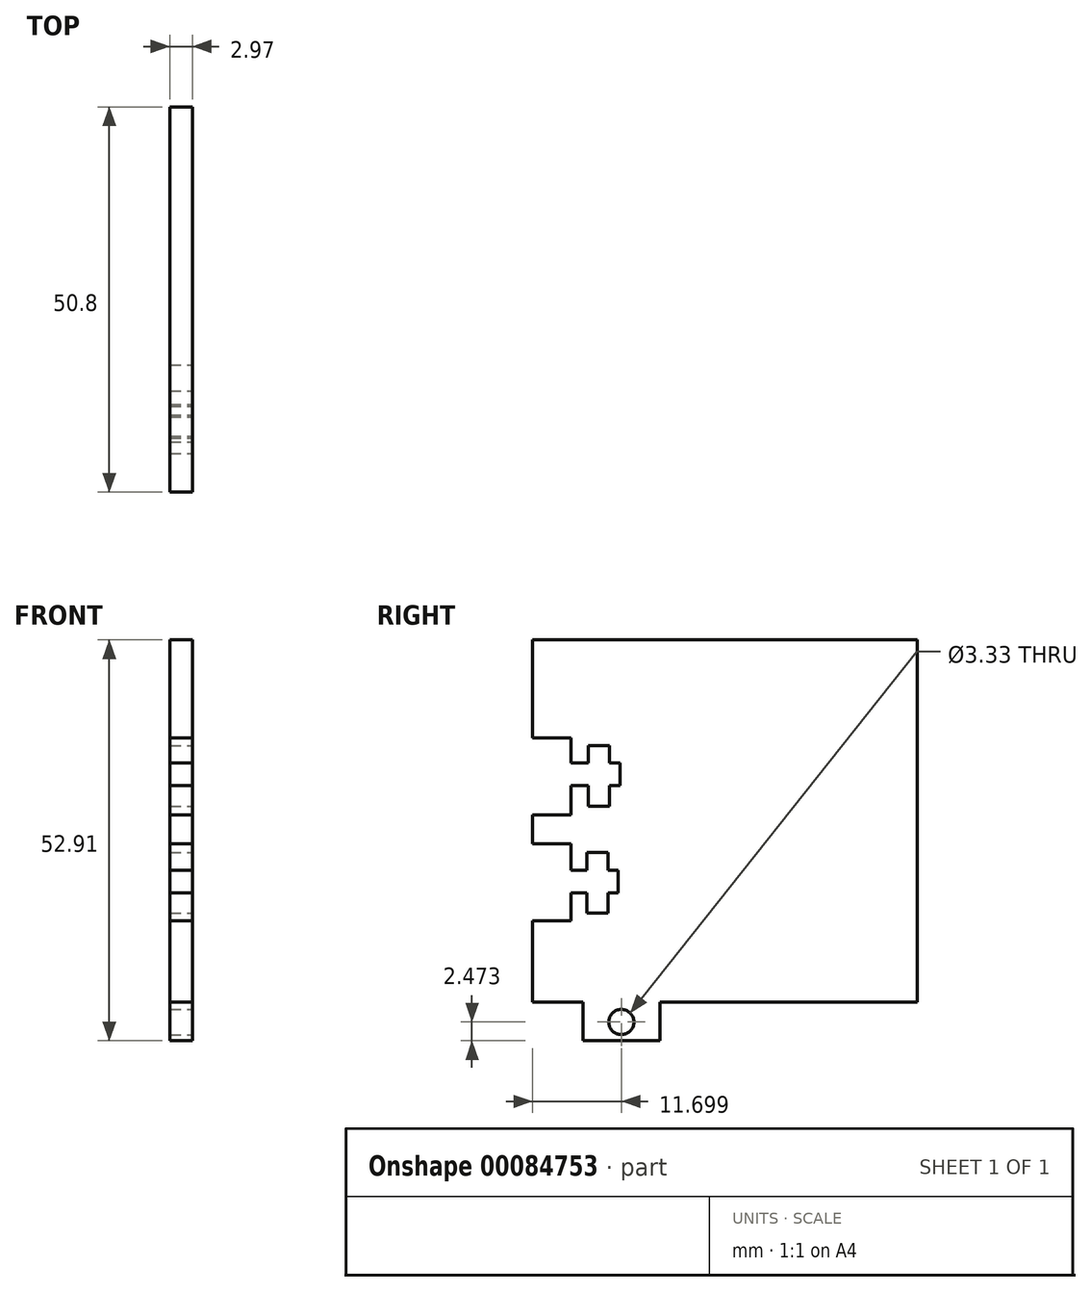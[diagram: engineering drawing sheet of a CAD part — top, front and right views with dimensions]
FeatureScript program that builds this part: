
annotation { "Feature Type Name" : "Feature", "Feature Type Description" : "" }
export const myFeature = defineFeature(function(context is Context, id is Id, definition is map)
    precondition{}
    {
        {
            var Q0;
            Q0=qCreatedBy(makeId("Right.planeOp"),FACE);
            var sketch = newSketch(context, id + "F0", { "sketchPlane" : qUnion([Q0])});
            skLineSegment(sketch, "E0.bottom", {"start": v(25.4, 25.4) * mm, "end": v(-25.4, 25.4) * mm});
            skLineSegment(sketch, "E0.top", {"start": v(25.4, -25.4) * mm, "end": v(-25.4, -25.4) * mm});
            skLineSegment(sketch, "E0.left", {"start": v(25.4, 25.4) * mm, "end": v(25.4, -25.4) * mm});
            skLineSegment(sketch, "E0.right", {"start": v(-25.4, 25.4) * mm, "end": v(-25.4, -25.4) * mm});
            skPoint(sketch, "E0.middle", {"position": v(0, 0) * mm});
            skSolve(sketch);
        }
        {
            var Q0;
            Q0 = qSketchRegion(id + "F0", true);
            extrude(context, id + "F1", {"entities" : qUnion([Q0]), "depth" : 2.97 * mm});
        }
        {
            var Q0;
            Q0=makeQuery(id+"F1.opExtrude","CAP_FACE",FACE,{"disambiguationData":[OSD([sQuery(id+"F0.wireOp",EDGE,"E0.bottom"),sQuery(id+"F0.wireOp",EDGE,"E0.top"),sQuery(id+"F0.wireOp",EDGE,"E0.left"),sQuery(id+"F0.wireOp",EDGE,"E0.right")])],"isStart":false});
            var sketch = newSketch(context, id + "F2", { "sketchPlane" : qUnion([Q0])});
            skLineSegment(sketch, "E1.bottom", {"start": v(-25.4, 12.46) * mm, "end": v(-20.32, 12.46) * mm});
            skLineSegment(sketch, "E1.top", {"start": v(-25.4, 2.3) * mm, "end": v(-20.32, 2.3) * mm});
            skLineSegment(sketch, "E1.left", {"start": v(-25.4, 12.46) * mm, "end": v(-25.4, 2.3) * mm});
            skLineSegment(sketch, "E1.right", {"start": v(-20.32, 12.46) * mm, "end": v(-20.32, 2.3) * mm});
            skLineSegment(sketch, "E2.bottom", {"start": v(-25.4, -1.5) * mm, "end": v(-20.32, -1.5) * mm});
            skLineSegment(sketch, "E2.top", {"start": v(-25.4, -11.67) * mm, "end": v(-20.32, -11.67) * mm});
            skLineSegment(sketch, "E2.left", {"start": v(-25.4, -1.5) * mm, "end": v(-25.4, -11.67) * mm});
            skLineSegment(sketch, "E2.right", {"start": v(-20.32, -1.5) * mm, "end": v(-20.32, -11.67) * mm});
            skSolve(sketch);
        }
        {
            var Q0;
            Q0 = qSketchRegion(id + "F2", true);
            extrude(context, id + "F3", {"entities" : qUnion([Q0]), "operationType" : NewBodyOperationType.REMOVE, "endBound" : BoundingType.THROUGH_ALL, "oppositeDirection" : true, "depth" : 25.4 * mm});
        }
        {
            var Q0;
            Q0=makeQuery(id+"F1.opExtrude","CAP_FACE",FACE,{"disambiguationData":[OSD([sQuery(id+"F0.wireOp",EDGE,"E0.bottom"),sQuery(id+"F0.wireOp",EDGE,"E0.top"),sQuery(id+"F0.wireOp",EDGE,"E0.left"),sQuery(id+"F0.wireOp",EDGE,"E0.right")])],"isStart":false});
            var sketch = newSketch(context, id + "F4", { "sketchPlane" : qUnion([Q0])});
            skLineSegment(sketch, "E3.bottom", {"start": v(-20.32, 9.15) * mm, "end": v(-13.87, 9.15) * mm});
            skLineSegment(sketch, "E3.top", {"start": v(-20.32, 6.17) * mm, "end": v(-13.87, 6.17) * mm});
            skLineSegment(sketch, "E3.left", {"start": v(-20.32, 9.15) * mm, "end": v(-20.32, 6.17) * mm});
            skLineSegment(sketch, "E3.right", {"start": v(-13.87, 9.15) * mm, "end": v(-13.87, 6.17) * mm});
            skLineSegment(sketch, "E4.bottom", {"start": v(-15.25, 11.45) * mm, "end": v(-18.04, 11.45) * mm});
            skLineSegment(sketch, "E4.top", {"start": v(-15.25, 3.45) * mm, "end": v(-18.04, 3.45) * mm});
            skLineSegment(sketch, "E4.left", {"start": v(-15.25, 11.45) * mm, "end": v(-15.25, 3.45) * mm});
            skLineSegment(sketch, "E4.right", {"start": v(-18.04, 11.45) * mm, "end": v(-18.04, 3.45) * mm});
            skLineSegment(sketch, "E5.bottom", {"start": v(-20.55, -4.98) * mm, "end": v(-14.1, -4.98) * mm});
            skLineSegment(sketch, "E5.top", {"start": v(-20.55, -7.96) * mm, "end": v(-14.1, -7.96) * mm});
            skLineSegment(sketch, "E5.left", {"start": v(-20.55, -4.98) * mm, "end": v(-20.55, -7.96) * mm});
            skLineSegment(sketch, "E5.right", {"start": v(-14.1, -4.98) * mm, "end": v(-14.1, -7.96) * mm});
            skLineSegment(sketch, "E6.bottom", {"start": v(-15.48, -2.68) * mm, "end": v(-18.28, -2.68) * mm});
            skLineSegment(sketch, "E6.top", {"start": v(-15.48, -10.69) * mm, "end": v(-18.28, -10.69) * mm});
            skLineSegment(sketch, "E6.left", {"start": v(-15.48, -2.68) * mm, "end": v(-15.48, -10.69) * mm});
            skLineSegment(sketch, "E6.right", {"start": v(-18.28, -2.68) * mm, "end": v(-18.28, -10.69) * mm});
            skSolve(sketch);
        }
        {
            var Q0;
            {var subQ0=sQuery(id+"F4.wireOp",EDGE,"E3.left");Q0=makeQuery(id+"F4.imprint","IMPRINT",FACE,{"disambiguationData":[TD([[makeQuery(id+"F4.imprint","IMPRINT",EDGE,{"derivedFrom":subQ0}),1.0]])]});}
            var Q1;
            {var subQ0=sQuery(id+"F4.wireOp",EDGE,"E4.right");var subQ1=sQuery(id+"F4.wireOp",EDGE,"E3.bottom");var subQ2=makeQuery(id+"F4.imprint","INTERSECT",VERTEX,{"derivedFrom":[subQ1,subQ0]});Q1=makeQuery(id+"F4.imprint","IMPRINT",FACE,{"disambiguationData":[TD([[makeQuery(id+"F4.imprint","IMPRINT",EDGE,{"disambiguationData":[TD([[subQ2,-1.0]])],"derivedFrom":subQ1}),-1.0]])]});}
            var Q2;
            {var subQ0=sQuery(id+"F4.wireOp",EDGE,"E3.right");Q2=makeQuery(id+"F4.imprint","IMPRINT",FACE,{"disambiguationData":[TD([[makeQuery(id+"F4.imprint","IMPRINT",EDGE,{"derivedFrom":subQ0}),-1.0]])]});}
            var Q3;
            {var subQ5=sQuery(id+"F4.wireOp",EDGE,"E4.bottom");Q3=makeQuery(id+"F4.imprint","IMPRINT",FACE,{"disambiguationData":[TD([[makeQuery(id+"F4.imprint","IMPRINT",EDGE,{"derivedFrom":subQ5}),1.0]])]});}
            var Q4;
            {var subQ5=sQuery(id+"F4.wireOp",EDGE,"E4.top");Q4=makeQuery(id+"F4.imprint","IMPRINT",FACE,{"disambiguationData":[TD([[makeQuery(id+"F4.imprint","IMPRINT",EDGE,{"derivedFrom":subQ5}),-1.0]])]});}
            var Q5;
            {var subQ5=sQuery(id+"F4.wireOp",EDGE,"E6.bottom");Q5=makeQuery(id+"F4.imprint","IMPRINT",FACE,{"disambiguationData":[TD([[makeQuery(id+"F4.imprint","IMPRINT",EDGE,{"derivedFrom":subQ5}),1.0]])]});}
            var Q6;
            {var subQ0=sQuery(id+"F4.wireOp",EDGE,"E6.right");var subQ1=sQuery(id+"F4.wireOp",EDGE,"E5.bottom");var subQ2=makeQuery(id+"F4.imprint","INTERSECT",VERTEX,{"derivedFrom":[subQ1,subQ0]});Q6=makeQuery(id+"F4.imprint","IMPRINT",FACE,{"disambiguationData":[TD([[makeQuery(id+"F4.imprint","IMPRINT",EDGE,{"disambiguationData":[TD([[subQ2,1.0]])],"derivedFrom":subQ1}),-1.0]])]});}
            var Q7;
            {var subQ0=sQuery(id+"F4.wireOp",EDGE,"E5.right");Q7=makeQuery(id+"F4.imprint","IMPRINT",FACE,{"disambiguationData":[TD([[makeQuery(id+"F4.imprint","IMPRINT",EDGE,{"derivedFrom":subQ0}),-1.0]])]});}
            var Q8;
            {var subQ0=sQuery(id+"F4.wireOp",EDGE,"E6.right");var subQ1=sQuery(id+"F4.wireOp",EDGE,"E5.bottom");var subQ2=makeQuery(id+"F4.imprint","INTERSECT",VERTEX,{"derivedFrom":[subQ1,subQ0]});Q8=makeQuery(id+"F4.imprint","IMPRINT",FACE,{"disambiguationData":[TD([[makeQuery(id+"F4.imprint","IMPRINT",EDGE,{"disambiguationData":[TD([[subQ2,-1.0]])],"derivedFrom":subQ1}),-1.0]])]});}
            var Q9;
            {var subQ5=sQuery(id+"F4.wireOp",EDGE,"E6.top");Q9=makeQuery(id+"F4.imprint","IMPRINT",FACE,{"disambiguationData":[TD([[makeQuery(id+"F4.imprint","IMPRINT",EDGE,{"derivedFrom":subQ5}),-1.0]])]});}
            extrude(context, id + "F5", {"entities" : qUnion([Q0, Q1, Q2, Q3, Q4, Q5, Q6, Q7, Q8, Q9]), "operationType" : NewBodyOperationType.REMOVE, "endBound" : BoundingType.THROUGH_ALL, "oppositeDirection" : true, "depth" : 25.4 * mm});
        }
        {
            var Q0;
            Q0=makeQuery(id+"F1.opExtrude","CAP_FACE",FACE,{"disambiguationData":[OSD([sQuery(id+"F0.wireOp",EDGE,"E0.bottom"),sQuery(id+"F0.wireOp",EDGE,"E0.top"),sQuery(id+"F0.wireOp",EDGE,"E0.left"),sQuery(id+"F0.wireOp",EDGE,"E0.right")])],"isStart":false});
            var sketch = newSketch(context, id + "F6", { "sketchPlane" : qUnion([Q0])});
            skLineSegment(sketch, "E7.bottom", {"start": v(25.4, -25.4) * mm, "end": v(-25.4, -25.4) * mm});
            skLineSegment(sketch, "E7.top", {"start": v(25.4, -22.43) * mm, "end": v(-25.4, -22.43) * mm});
            skLineSegment(sketch, "E7.left", {"start": v(25.4, -25.4) * mm, "end": v(25.4, -22.43) * mm});
            skLineSegment(sketch, "E7.right", {"start": v(-25.4, -25.4) * mm, "end": v(-25.4, -22.43) * mm});
            skSolve(sketch);
        }
        {
            var Q0;
            Q0 = qSketchRegion(id + "F6", true);
            extrude(context, id + "F7", {"entities" : qUnion([Q0]), "operationType" : NewBodyOperationType.REMOVE, "oppositeDirection" : true, "depth" : 25.4 * mm});
        }
        {
            var Q0;
            Q0=makeQuery(id+"F1.opExtrude","CAP_FACE",FACE,{"disambiguationData":[OSD([sQuery(id+"F0.wireOp",EDGE,"E0.bottom"),sQuery(id+"F0.wireOp",EDGE,"E0.top"),sQuery(id+"F0.wireOp",EDGE,"E0.left"),sQuery(id+"F0.wireOp",EDGE,"E0.right")])],"isStart":false});
            var sketch = newSketch(context, id + "F8", { "sketchPlane" : qUnion([Q0])});
            skLineSegment(sketch, "E8.bottom", {"start": v(-18.78, -22.43) * mm, "end": v(-8.62, -22.43) * mm});
            skLineSegment(sketch, "E8.top", {"start": v(-18.78, -27.5) * mm, "end": v(-8.62, -27.5) * mm});
            skLineSegment(sketch, "E8.left", {"start": v(-18.78, -22.43) * mm, "end": v(-18.78, -27.5) * mm});
            skLineSegment(sketch, "E8.right", {"start": v(-8.62, -22.43) * mm, "end": v(-8.62, -27.5) * mm});
            skCircle(sketch, "E9", {"center": v(-13.7, -25.04) * mm, "radius": 1.66 * mm});
            skPoint(sketch, "E9.centerSnap0", {"position": v(-13.7, -22.43) * mm});
            skSolve(sketch);
        }
        {
            var Q0;
            Q0 = qSketchRegion(id + "F8", true);
            extrude(context, id + "F9", {"entities" : qUnion([Q0]), "operationType" : NewBodyOperationType.ADD, "oppositeDirection" : true, "depth" : 2.97 * mm});
        }
    });
